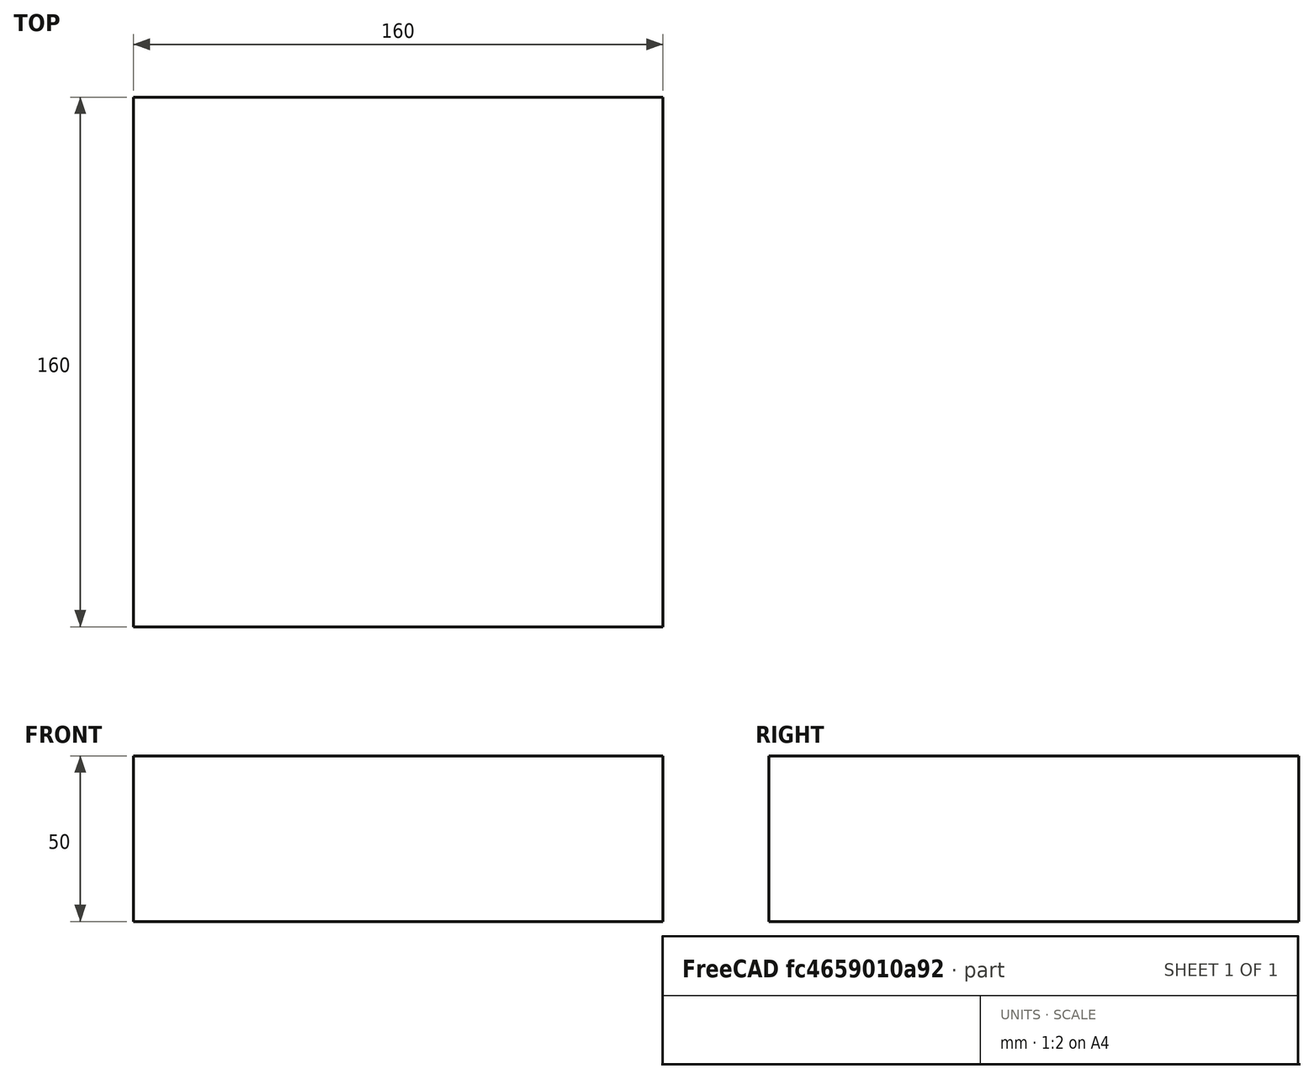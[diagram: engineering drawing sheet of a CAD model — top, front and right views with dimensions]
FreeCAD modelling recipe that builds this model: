
FCSTD DOCUMENT  (FreeCAD 0.15R4671 (Git))
Label: Square Bar 160 EN10059 S235JR
License: All rights reserved
LicenseURL: http://en.wikipedia.org/wiki/All_rights_reserved
objects: Sketcher::SketchObject×1, Part::Extrusion×1
note: 2 computed .brp shape members not serialized (recipe doc carries the construction recipe); baked Part::Feature solids carry a one-line shape summary decoded from their .brp

FEATURE [Sketcher::SketchObject] Sketch
  sketch-geometry (4):
    g0: LineSegment StartX=-80 StartY=-80 StartZ=0 EndX=80 EndY=-80 EndZ=0
    g1: LineSegment StartX=80 StartY=-80 StartZ=0 EndX=80 EndY=80 EndZ=0
    g2: LineSegment StartX=80 StartY=80 StartZ=0 EndX=-80 EndY=80 EndZ=0
    g3: LineSegment StartX=-80 StartY=80 StartZ=0 EndX=-80 EndY=-80 EndZ=0
  constraints (12):
    c: Coincident(g0,g1)
    c: Coincident(g1,g2)
    c: Coincident(g2,g3)
    c: Coincident(g3,g0)
    c: Horizontal(g0)
    c: Horizontal(g2)
    c: Vertical(g1)
    c: Vertical(g3)
    c: Symmetric(g1,g0,g-1)
    c: Symmetric(g2,g1,g-2)
    c: Equal(g1,g2)
    c: DistanceY(g1) = 160
FEATURE [Part::Extrusion] Extrude  label="Square Bar 160 EN10059 S235JR"
  Base = -> Sketch
  Dir = (0,0,50)
  Solid = true
